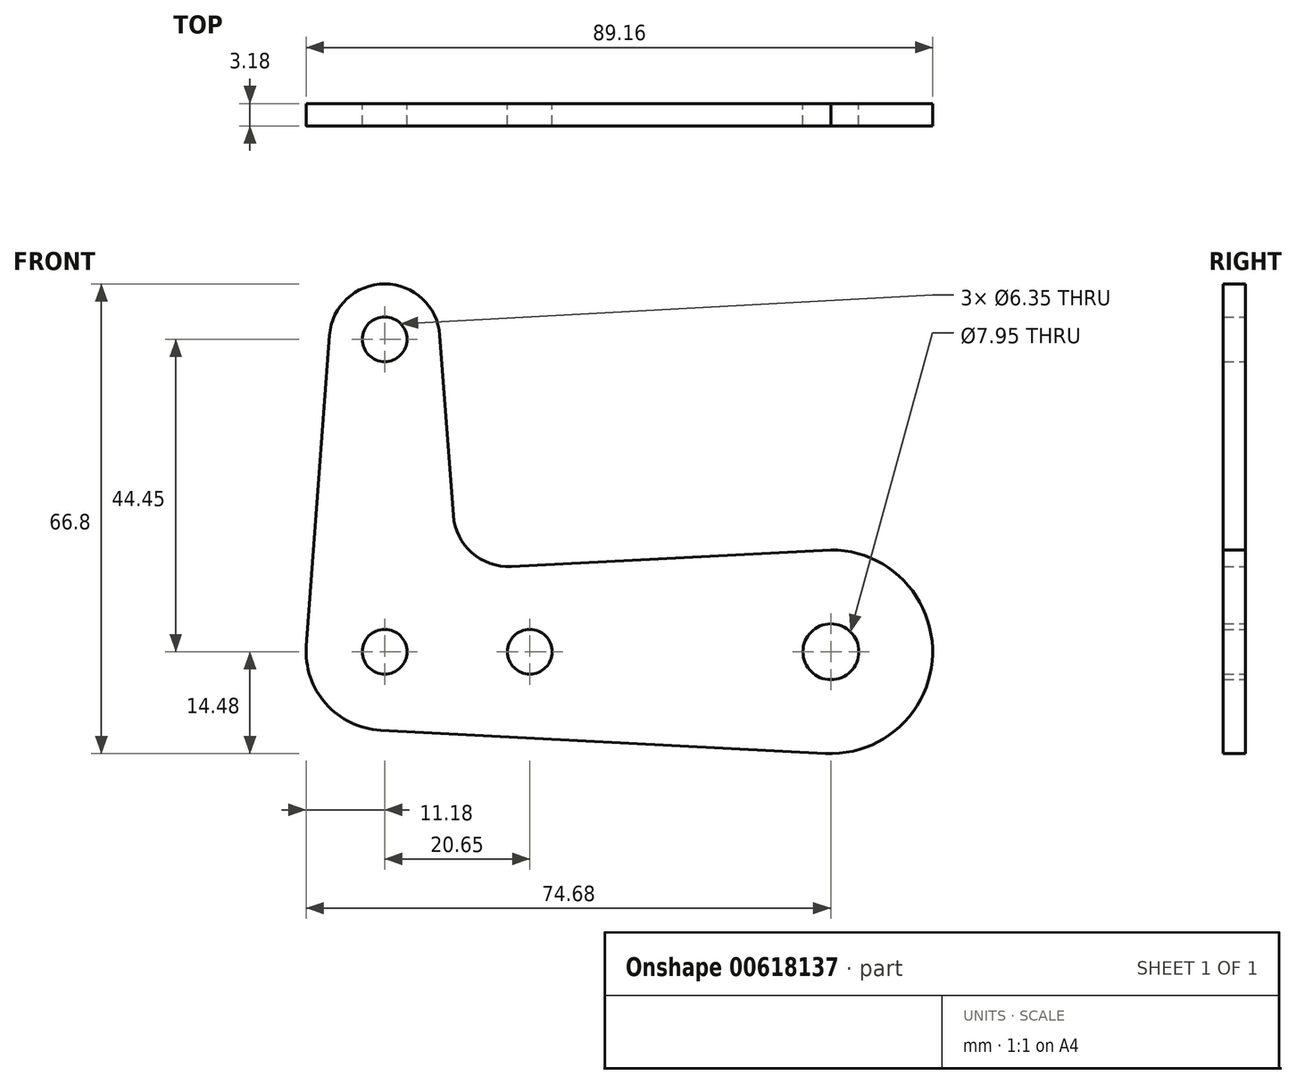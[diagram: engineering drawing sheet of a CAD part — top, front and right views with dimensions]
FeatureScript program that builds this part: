
annotation { "Feature Type Name" : "Feature", "Feature Type Description" : "" }
export const myFeature = defineFeature(function(context is Context, id is Id, definition is map)
    precondition{}
    {
        {
            var Q0;
            Q0=qCreatedBy(makeId("Front.planeOp"),FACE);
            var sketch = newSketch(context, id + "F0", { "sketchPlane" : qUnion([Q0])});
            skCircle(sketch, "E0", {"center": v(0, 0) * mm, "radius": 3.98 * mm});
            skLineSegment(sketch, "E1", {"start": v(0, 0) * mm, "end": v(-63.5, 0) * mm, "construction": true});
            skLineSegment(sketch, "E2", {"start": v(-63.5, 0) * mm, "end": v(-63.5, 44.45) * mm, "construction": true});
            skCircle(sketch, "E3", {"center": v(-63.5, 44.45) * mm, "radius": 3.18 * mm});
            skCircle(sketch, "E4", {"center": v(-63.5, 0) * mm, "radius": 3.18 * mm});
            skCircle(sketch, "E5", {"center": v(-42.85, 0) * mm, "radius": 3.18 * mm});
            skCircle(sketch, "E6", {"center": v(0, 0) * mm, "radius": 14.48 * mm});
            skCircle(sketch, "E7", {"center": v(-63.5, 44.45) * mm, "radius": 7.87 * mm});
            skCircle(sketch, "E8", {"center": v(-63.5, 0) * mm, "radius": 11.18 * mm});
            skLineSegment(sketch, "E9", {"start": v(-71.35, 45.03) * mm, "end": v(-74.7, 0) * mm});
            skLineSegment(sketch, "E10", {"start": v(-64.08, -11.16) * mm, "end": v(0, -14.5) * mm});
            skLineSegment(sketch, "E11", {"start": v(0, 14.48) * mm, "end": v(-45.48, 12.12) * mm});
            skLineSegment(sketch, "E12", {"start": v(-55.65, 45.03) * mm, "end": v(-53.74, 19.4) * mm});
            skLineSegment(sketch, "E13.trimOffspring", {"start": v(-63.5, 11.2) * mm, "end": v(-64.08, 11.16) * mm});
            skPoint(sketch, "E14.visualSharp", {"position": v(-53.17, 11.73) * mm});
            skArc(sketch, "E14.filletArc", {"start": v(-53.74, 19.4) * mm, "mid": v(-51.1, 14.08) * mm, "end": v(-45.48, 12.12) * mm});
            skSolve(sketch);
        }
        {
            var Q0;
            Q0=makeQuery(id+"F0.imprint","IMPRINT",FACE,{"disambiguationData":[TD([[makeQuery(id+"F0.imprint","IMPRINT",EDGE,{"derivedFrom":sQuery(id+"F0.wireOp",EDGE,"E3")}),-1.0]])]});
            var Q1;
            Q1=makeQuery(id+"F0.imprint","IMPRINT",FACE,{"disambiguationData":[TD([[makeQuery(id+"F0.imprint","IMPRINT",EDGE,{"derivedFrom":sQuery(id+"F0.wireOp",EDGE,"E5")}),-1.0]])]});
            var Q2;
            Q2=makeQuery(id+"F0.imprint","IMPRINT",FACE,{"disambiguationData":[TD([[makeQuery(id+"F0.imprint","IMPRINT",EDGE,{"derivedFrom":sQuery(id+"F0.wireOp",EDGE,"E4")}),-1.0]])]});
            var Q3;
            Q3=makeQuery(id+"F0.imprint","IMPRINT",FACE,{"disambiguationData":[TD([[makeQuery(id+"F0.imprint","IMPRINT",EDGE,{"derivedFrom":sQuery(id+"F0.wireOp",EDGE,"E0")}),-1.0]])]});
            extrude(context, id + "F1", {"entities" : qUnion([Q0, Q1, Q2, Q3]), "depth" : 3.17 * mm, "offsetDistance" : 25.4 * mm});
        }
    });
